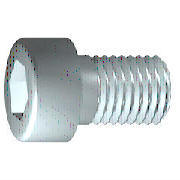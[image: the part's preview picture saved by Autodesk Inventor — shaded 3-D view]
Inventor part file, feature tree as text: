
AUTODESK INVENTOR PART (.ipt)
format: ipt  version: 2018 (Build 220112000, 112)  size: 182,784 bytes
history: native  units: mm (DEFAULTED — no unit token found)
features: sketch x2, extrude x1, plane x1, fillet x1
ambient origin geometry x7: Origin, YZ Plane, XY Plane, X Axis, Y Axis, Z Axis, Center Point
bodies: Solid1 (feature_tree), Body (feature_tree)
feature tree (5):
  extrude  "Slot"  Depth=5.0mm
  plane  "Work Plane1"
  fillet  "Fillet2"  Radius=5.0mm
  sketch  "Sketch1"  dims[d1=22.0mm d2=0.49086mm d3=5.0mm]
  sketch  "Sketch2"  dims[d4=2.5mm d5=60.0deg d6=5.0mm d7=5.0mm d8=4.618802mm d9=8.5mm d10=90.0deg d11=10.0mm d12=0.0mm d13=22.0mm d14=0.0mm d15=0.49076mm d16=0.49076mm d17=0.5mm d19=0.0mm d26=45.0mm d27=45.0deg d28=0.0mm d29=0.0mm d30=0.1mm]
